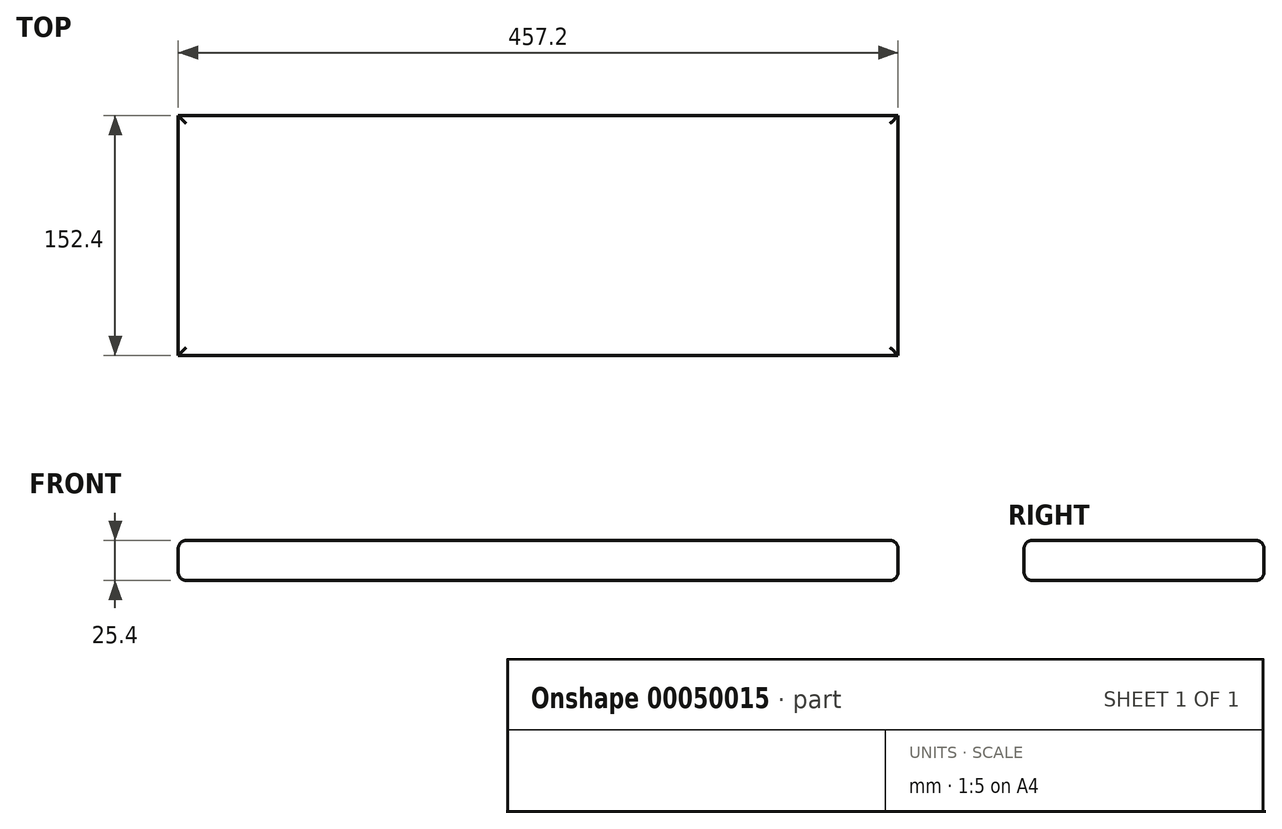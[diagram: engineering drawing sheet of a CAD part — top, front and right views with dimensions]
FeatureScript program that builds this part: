
annotation { "Feature Type Name" : "Feature", "Feature Type Description" : "" }
export const myFeature = defineFeature(function(context is Context, id is Id, definition is map)
    precondition{}
    {
        {
            var Q0;
            Q0=qCreatedBy(makeId("Top.planeOp"),FACE);
            var sketch = newSketch(context, id + "F0", { "sketchPlane" : qUnion([Q0])});
            skLineSegment(sketch, "E0.bottom", {"start": v(0, 0) * mm, "end": v(457.2, 0) * mm});
            skLineSegment(sketch, "E0.top", {"start": v(0, -152.4) * mm, "end": v(457.2, -152.4) * mm});
            skLineSegment(sketch, "E0.left", {"start": v(0, 0) * mm, "end": v(0, -152.4) * mm});
            skLineSegment(sketch, "E0.right", {"start": v(457.2, 0) * mm, "end": v(457.2, -152.4) * mm});
            skSolve(sketch);
        }
        {
            var Q0;
            Q0=makeQuery(id+"F0.imprint","IMPRINT",FACE,{"disambiguationData":[TD([[makeQuery(id+"F0.imprint","IMPRINT",EDGE,{"derivedFrom":sQuery(id+"F0.wireOp",EDGE,"E0.bottom")}),-1.0]])]});
            extrude(context, id + "F1", {"entities" : qUnion([Q0]), "depth" : 25.4 * mm});
        }
        {
            var Q0;
            Q0=makeQuery(id+"F1.opExtrude","CAP_EDGE",EDGE,{"disambiguationData":[OSD([sQuery(id+"F0.wireOp",EDGE,"E0.left")])],"isStart":false});
            var Q1;
            Q1=makeQuery(id+"F1.opExtrude","CAP_EDGE",EDGE,{"disambiguationData":[OSD([sQuery(id+"F0.wireOp",EDGE,"E0.top")])],"isStart":false});
            var Q2;
            Q2=makeQuery(id+"F1.opExtrude","CAP_EDGE",EDGE,{"disambiguationData":[OSD([sQuery(id+"F0.wireOp",EDGE,"E0.bottom")])],"isStart":false});
            var Q3;
            Q3=makeQuery(id+"F1.opExtrude","CAP_EDGE",EDGE,{"disambiguationData":[OSD([sQuery(id+"F0.wireOp",EDGE,"E0.right")])],"isStart":false});
            fillet(context, id + "F2", {"entities" : qUnion([Q0, Q1, Q2, Q3]), "radius" : 5.08 * mm, "tangentPropagation" : true, "allowEdgeOverflow" : false});
        }
        {
            var Q0;
            Q0=makeQuery(id+"F1.opExtrude","CAP_EDGE",EDGE,{"disambiguationData":[OSD([sQuery(id+"F0.wireOp",EDGE,"E0.top")])],"isStart":true});
            var Q1;
            Q1=makeQuery(id+"F1.opExtrude","CAP_EDGE",EDGE,{"disambiguationData":[OSD([sQuery(id+"F0.wireOp",EDGE,"E0.right")])],"isStart":true});
            var Q2;
            Q2=makeQuery(id+"F1.opExtrude","CAP_EDGE",EDGE,{"disambiguationData":[OSD([sQuery(id+"F0.wireOp",EDGE,"E0.bottom")])],"isStart":true});
            var Q3;
            Q3=makeQuery(id+"F1.opExtrude","CAP_EDGE",EDGE,{"disambiguationData":[OSD([sQuery(id+"F0.wireOp",EDGE,"E0.left")])],"isStart":true});
            fillet(context, id + "F3", {"entities" : qUnion([Q0, Q1, Q2, Q3]), "radius" : 5.08 * mm, "tangentPropagation" : true, "allowEdgeOverflow" : false});
        }
    });
